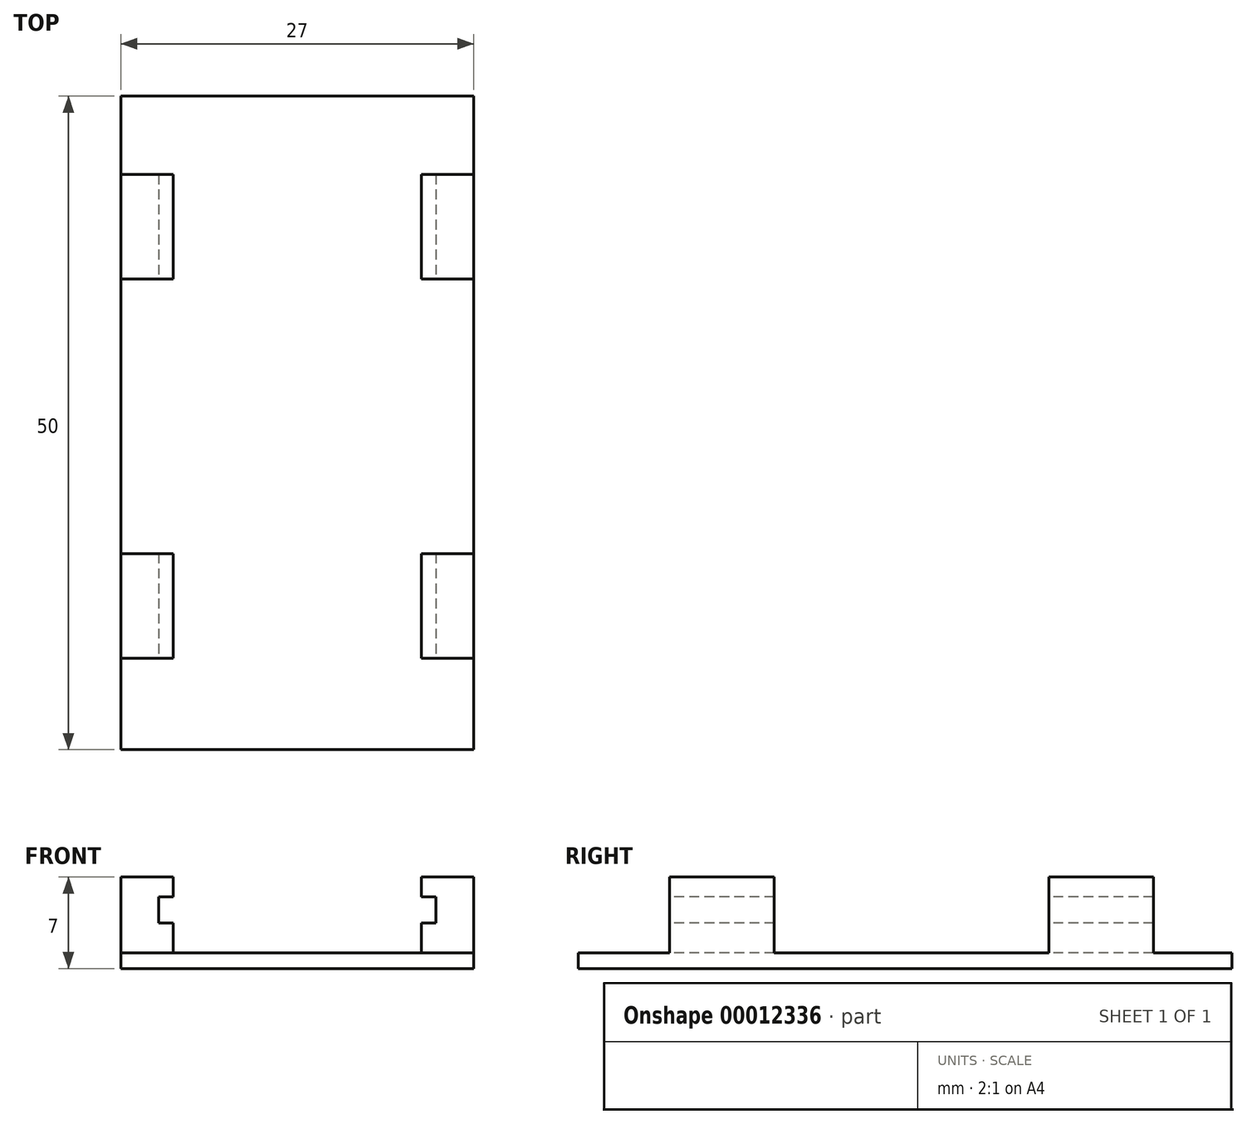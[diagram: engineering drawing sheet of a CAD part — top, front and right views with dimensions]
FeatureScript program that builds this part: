
annotation { "Feature Type Name" : "Feature", "Feature Type Description" : "" }
export const myFeature = defineFeature(function(context is Context, id is Id, definition is map)
    precondition{}
    {
        {
            var Q0;
            Q0=qCreatedBy(makeId("Top.planeOp"),FACE);
            var sketch = newSketch(context, id + "F0", { "sketchPlane" : qUnion([Q0])});
            skLineSegment(sketch, "E0.rect.bottom", {"start": v(13.5, 25) * mm, "end": v(-13.5, 25) * mm});
            skLineSegment(sketch, "E0.rect.top", {"start": v(13.5, -25) * mm, "end": v(-13.5, -25) * mm});
            skLineSegment(sketch, "E0.rect.left", {"start": v(13.5, 25) * mm, "end": v(13.5, -25) * mm});
            skLineSegment(sketch, "E0.rect.right", {"start": v(-13.5, 25) * mm, "end": v(-13.5, -25) * mm});
            skPoint(sketch, "E0.rect.middle", {"position": v(0, 0) * mm});
            skPoint(sketch, "E1.visualSharp", {"position": v(-13.5, 25) * mm});
            skLineSegment(sketch, "E1.filletArc", {"start": v(-13.5, 25) * mm, "end": v(-13.5, 25) * mm});
            skPoint(sketch, "E2.visualSharp", {"position": v(13.5, 25) * mm});
            skLineSegment(sketch, "E2.filletArc", {"start": v(13.5, 25) * mm, "end": v(13.5, 25) * mm});
            skPoint(sketch, "E3.visualSharp", {"position": v(13.5, -25) * mm});
            skLineSegment(sketch, "E3.filletArc", {"start": v(13.5, -25) * mm, "end": v(13.5, -25) * mm});
            skPoint(sketch, "E4.visualSharp", {"position": v(-13.5, -25) * mm});
            skLineSegment(sketch, "E4.filletArc", {"start": v(-13.5, -25) * mm, "end": v(-13.5, -25) * mm});
            skSolve(sketch);
        }
        {
            var Q0;
            Q0=makeQuery(id+"F0.imprint","IMPRINT",FACE,{"disambiguationData":[TD([[makeQuery(id+"F0.imprint","IMPRINT",EDGE,{"derivedFrom":sQuery(id+"F0.wireOp",EDGE,"E0.rect.bottom")}),1.0]])]});
            extrude(context, id + "F1", {"entities" : qUnion([Q0]), "depth" : 7 * mm});
        }
        {
            var Q0;
            Q0=makeQuery(id+"F1.opExtrude","CAP_FACE",FACE,{"disambiguationData":[OSD([sQuery(id+"F0.wireOp",EDGE,"E0.rect.bottom"),sQuery(id+"F0.wireOp",EDGE,"E0.rect.top"),sQuery(id+"F0.wireOp",EDGE,"E0.rect.left"),sQuery(id+"F0.wireOp",EDGE,"E0.rect.right"),sQuery(id+"F0.wireOp",EDGE,"E1.filletArc"),sQuery(id+"F0.wireOp",EDGE,"E2.filletArc"),sQuery(id+"F0.wireOp",EDGE,"E3.filletArc"),sQuery(id+"F0.wireOp",EDGE,"E4.filletArc")])],"isStart":false});
            shell(context, id + "F2", {"entities" : qUnion([Q0]), "thickness" : 5 * mm});
        }
        {
            var Q0;
            Q0=makeQuery(id+"F1.opExtrude","SWEPT_FACE",FACE,{"disambiguationData":[OSD([sQuery(id+"F0.wireOp",EDGE,"E0.rect.top")])]});
            var sketch = newSketch(context, id + "F3", { "sketchPlane" : qUnion([Q0])});
            skLineSegment(sketch, "E5", {"start": v(0, 0) * mm, "end": v(0, 8.93) * mm, "construction": true});
            skLineSegment(sketch, "E6.rect.bottom", {"start": v(10.6, 5.47) * mm, "end": v(-10.6, 5.47) * mm, "construction": true});
            skLineSegment(sketch, "E6.rect.top", {"start": v(10.6, 3.47) * mm, "end": v(-10.6, 3.47) * mm, "construction": true});
            skLineSegment(sketch, "E6.rect.left", {"start": v(10.6, 5.47) * mm, "end": v(10.6, 3.47) * mm, "construction": true});
            skLineSegment(sketch, "E6.rect.right", {"start": v(-10.6, 5.47) * mm, "end": v(-10.6, 3.47) * mm, "construction": true});
            skPoint(sketch, "E6.rect.middle", {"position": v(0, 4.47) * mm});
            skLineSegment(sketch, "E7.rect.bottom", {"start": v(10.6, 5.47) * mm, "end": v(-10.6, 5.47) * mm});
            skLineSegment(sketch, "E7.rect.top", {"start": v(10.6, 3.47) * mm, "end": v(-10.6, 3.47) * mm});
            skLineSegment(sketch, "E7.rect.left", {"start": v(10.6, 5.47) * mm, "end": v(10.6, 3.47) * mm});
            skLineSegment(sketch, "E7.rect.right", {"start": v(-10.6, 5.47) * mm, "end": v(-10.6, 3.47) * mm});
            skSolve(sketch);
        }
        {
            var Q0;
            Q0=qSketchRegion(id+"F3",true);
            extrude(context, id + "F4", {"entities" : qUnion([Q0]), "operationType" : NewBodyOperationType.REMOVE, "endBound" : BoundingType.THROUGH_ALL, "oppositeDirection" : true, "depth" : 25 * mm});
        }
        {
            var Q0;
            Q0=makeQuery(id+"F3.imprint","IMPRINT",FACE,{"disambiguationData":[TD([[makeQuery(id+"F3.imprint","IMPRINT",EDGE,{"derivedFrom":sQuery(id+"F3.wireOp",EDGE,"E7.rect.bottom")}),-1.0]])]});
            var sketch = newSketch(context, id + "F5", { "sketchPlane" : qUnion([Q0])});
            skLineSegment(sketch, "E8.rect.bottom", {"start": v(9.5, 21.2) * mm, "end": v(-9.5, 21.2) * mm});
            skLineSegment(sketch, "E8.rect.top", {"start": v(9.5, 1.2) * mm, "end": v(-9.5, 1.2) * mm});
            skLineSegment(sketch, "E8.rect.left", {"start": v(9.5, 21.2) * mm, "end": v(9.5, 1.2) * mm});
            skLineSegment(sketch, "E8.rect.right", {"start": v(-9.5, 21.2) * mm, "end": v(-9.5, 1.2) * mm});
            skPoint(sketch, "E8.rect.middle", {"position": v(0, 11.2) * mm});
            skSolve(sketch);
        }
        {
            var Q0;
            Q0=qSketchRegion(id+"F5",true);
            extrude(context, id + "F6", {"entities" : qUnion([Q0]), "operationType" : NewBodyOperationType.REMOVE, "endBound" : BoundingType.THROUGH_ALL, "oppositeDirection" : true, "depth" : 25 * mm});
        }
        {
            var Q0;
            Q0=makeQuery(id+"F6.boolean.opBoolean","COPY",FACE,{"derivedFrom":makeQuery(id+"F6.opExtrude","SWEPT_FACE",FACE,{"disambiguationData":[OSD([sQuery(id+"F5.wireOp",EDGE,"E8.rect.top")])]})});
            cPlane(context, id + "F7", {"entities" : qUnion([Q0]), "cplaneType" : CPlaneType.OFFSET, "offset" : 0 * mm, "width" : 150 * mm, "height" : 150 * mm});
        }
        {
            var Q0;
            Q0=qCreatedBy(id+"F7.planeOp",FACE);
            var sketch = newSketch(context, id + "F8", { "sketchPlane" : qUnion([Q0])});
            skLineSegment(sketch, "E9", {"start": v(-23.9, 19) * mm, "end": v(26.1, 19) * mm});
            skLineSegment(sketch, "E10.0", {"start": v(-23.9, 11) * mm, "end": v(26.1, 11) * mm});
            skLineSegment(sketch, "E11", {"start": v(-23.9, 11) * mm, "end": v(-23.9, -10) * mm});
            skLineSegment(sketch, "E12", {"start": v(-23.9, -10) * mm, "end": v(26.1, -10) * mm});
            skLineSegment(sketch, "E13", {"start": v(26.1, -10) * mm, "end": v(26.1, 11) * mm});
            skLineSegment(sketch, "E14", {"start": v(-23.9, 19) * mm, "end": v(-23.9, 29.87) * mm});
            skLineSegment(sketch, "E15", {"start": v(-23.9, 29.87) * mm, "end": v(26.1, 29.87) * mm});
            skLineSegment(sketch, "E16", {"start": v(26.1, 29.87) * mm, "end": v(26.1, 19) * mm});
            skLineSegment(sketch, "E17", {"start": v(-24.46, -18) * mm, "end": v(26.7, -18) * mm});
            skLineSegment(sketch, "E18", {"start": v(26.7, -18) * mm, "end": v(26.7, -38) * mm});
            skLineSegment(sketch, "E19", {"start": v(26.7, -38) * mm, "end": v(-24.46, -38) * mm});
            skLineSegment(sketch, "E20", {"start": v(-24.46, -38) * mm, "end": v(-24.46, -18) * mm});
            skSolve(sketch);
        }
        {
            var Q0;
            Q0=qSketchRegion(id+"F8",true);
            extrude(context, id + "F9", {"entities" : qUnion([Q0]), "operationType" : NewBodyOperationType.REMOVE, "depth" : 25 * mm});
        }
        {
            var Q0;
            Q0=makeQuery(id+"F1.opExtrude","SWEPT_BODY",BODY,{"disambiguationData":[OSD([sQuery(id+"F0.wireOp",EDGE,"E0.rect.bottom"),sQuery(id+"F0.wireOp",EDGE,"E0.rect.top"),sQuery(id+"F0.wireOp",EDGE,"E0.rect.left"),sQuery(id+"F0.wireOp",EDGE,"E0.rect.right")])]});
            var Q1;
            Q1=sQuery(id+"F8.wireOp",EDGE,"E15");
            transform(context, id + "F10", {"entities" : qUnion([Q0]), "transformType" : TransformType.TRANSLATION_ENTITY, "oppositeDirectionEntity" : false, "transformLine" : qUnion([Q1]), "makeCopy" : true});
        }
        {
            var Q0;
            Q0=makeQuery(id+"F10.opPattern","COPY",BODY,{"derivedFrom":makeQuery(id+"F1.opExtrude","SWEPT_BODY",BODY,{"disambiguationData":[OSD([sQuery(id+"F0.wireOp",EDGE,"E0.rect.bottom"),sQuery(id+"F0.wireOp",EDGE,"E0.rect.top"),sQuery(id+"F0.wireOp",EDGE,"E0.rect.left"),sQuery(id+"F0.wireOp",EDGE,"E0.rect.right")])]}),"instanceName":"1"});
            deleteBodies(context, id + "F11", {"entities" : qUnion([Q0])});
        }
    });
